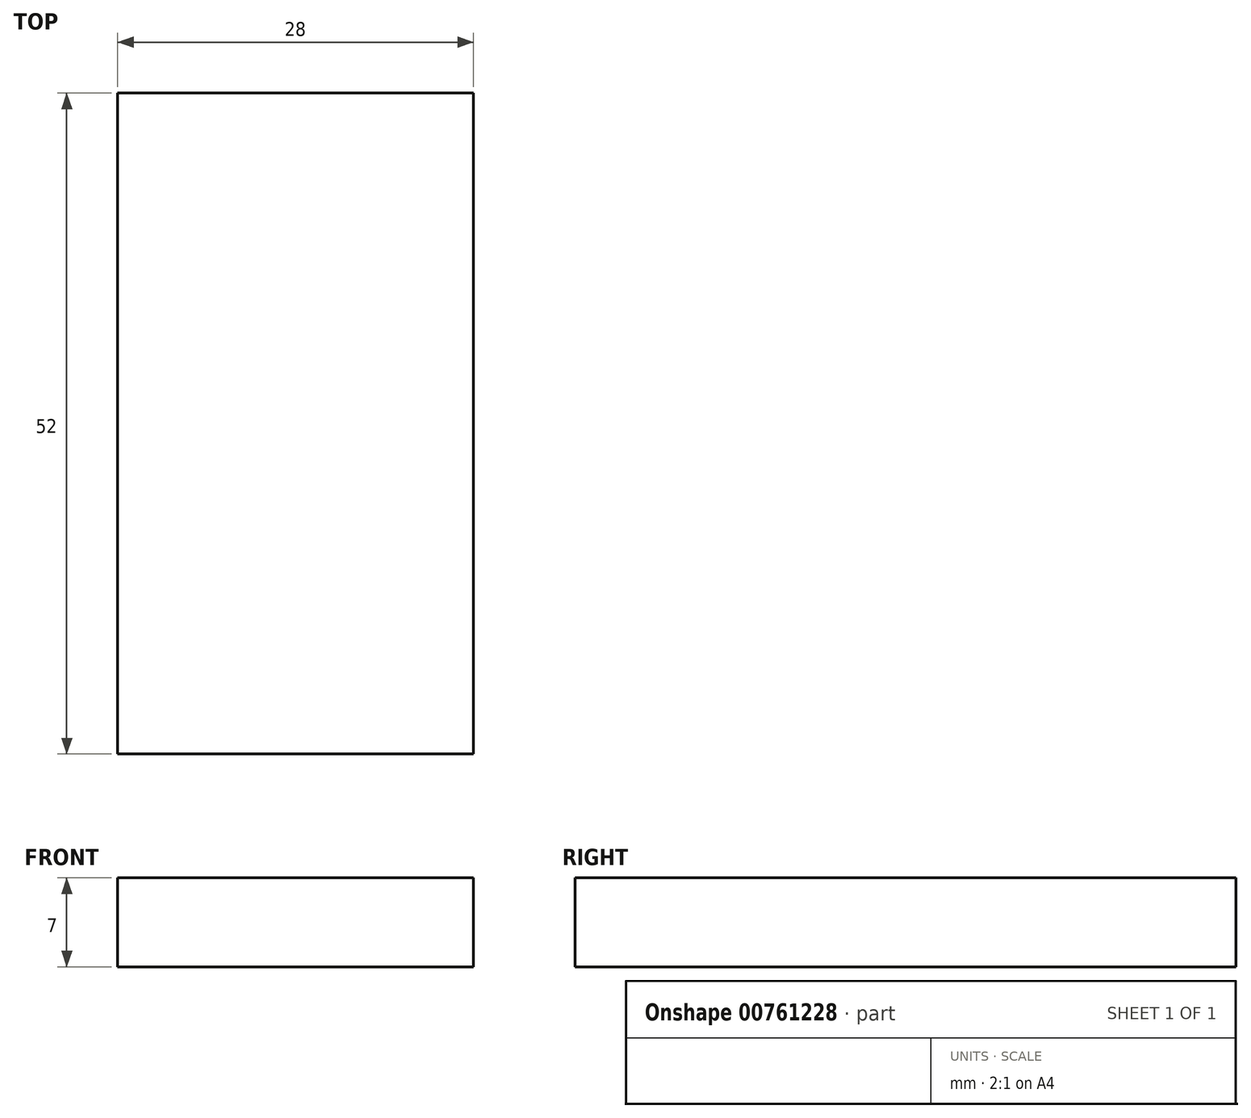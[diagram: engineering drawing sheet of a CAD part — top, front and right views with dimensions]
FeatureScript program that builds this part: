
annotation { "Feature Type Name" : "Feature", "Feature Type Description" : "" }
export const myFeature = defineFeature(function(context is Context, id is Id, definition is map)
    precondition{}
    {
        {
            var Q0;
            Q0=qCreatedBy(makeId("Top.planeOp"),FACE);
            var sketch = newSketch(context, id + "F0", { "sketchPlane" : qUnion([Q0])});
            skLineSegment(sketch, "E0.bottom", {"start": v(-32.45, -29.13) * mm, "end": v(-4.45, -29.13) * mm});
            skLineSegment(sketch, "E0.top", {"start": v(-32.45, 22.87) * mm, "end": v(-4.45, 22.87) * mm});
            skLineSegment(sketch, "E0.left", {"start": v(-32.45, -29.13) * mm, "end": v(-32.45, 22.87) * mm});
            skLineSegment(sketch, "E0.right", {"start": v(-4.45, -29.13) * mm, "end": v(-4.45, 22.87) * mm});
            skSolve(sketch);
        }
        {
            var Q0;
            Q0 = qSketchRegion(id + "F0", true);
            extrude(context, id + "F1", {"entities" : qUnion([Q0]), "depth" : 7 * mm, "offsetDistance" : 25 * mm});
        }
    });
